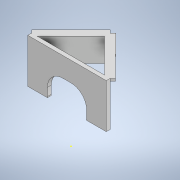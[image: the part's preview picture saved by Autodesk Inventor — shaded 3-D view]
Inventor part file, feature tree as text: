
AUTODESK INVENTOR PART (.ipt)
format: ipt  version: 2020 (Build 240168000, 168)  size: 174,592 bytes
history: native  units: mm
features: sketch x6, extrude x5
ambient origin geometry x8: Origin, YZ Plane, XZ Plane, XY Plane, X Axis, Y Axis, Z Axis, Center Point
bodies: Solid1 (feature_tree)
feature tree (11):
  extrude  "Extrusion1"  Depth=100.0mm
  extrude  "Extrusion2"  TaperAngle=45.0deg  [1 undecoded]
  extrude  "Extrusion6"  Depth=5.0mm
  extrude  "Extrusion9"  Depth=50.0mm
  sketch  "Sketch12"  dims[d22=50.0mm d23=20.0mm]
  extrude  "Extrusion10"  Depth=20.0mm
  sketch  "Sketch1"  dims[d0=100.0mm d1=200.0mm]
  sketch  "Sketch2"  dims[d2=5.0mm d3=0.0mm d4=45.0deg]
  sketch  "Sketch6"  dims[d5=5.0mm d6=5.0mm]
  sketch  "Sketch10"  dims[d7=30.0mm d8=0.0mm d21=50.0mm]
  sketch  "Sketch13"  dims[d24=5.0mm d25=0.0mm d33=5.0mm d34=5.0mm d36=3.0mm d37=0.0mm d38=0.0mm d39=0.0mm]
note: 1 required parameter value undecoded (feature->parameter linkage not recoverable at this tier; creation-order binding heuristic only, values carry confidence <= 0.55)
